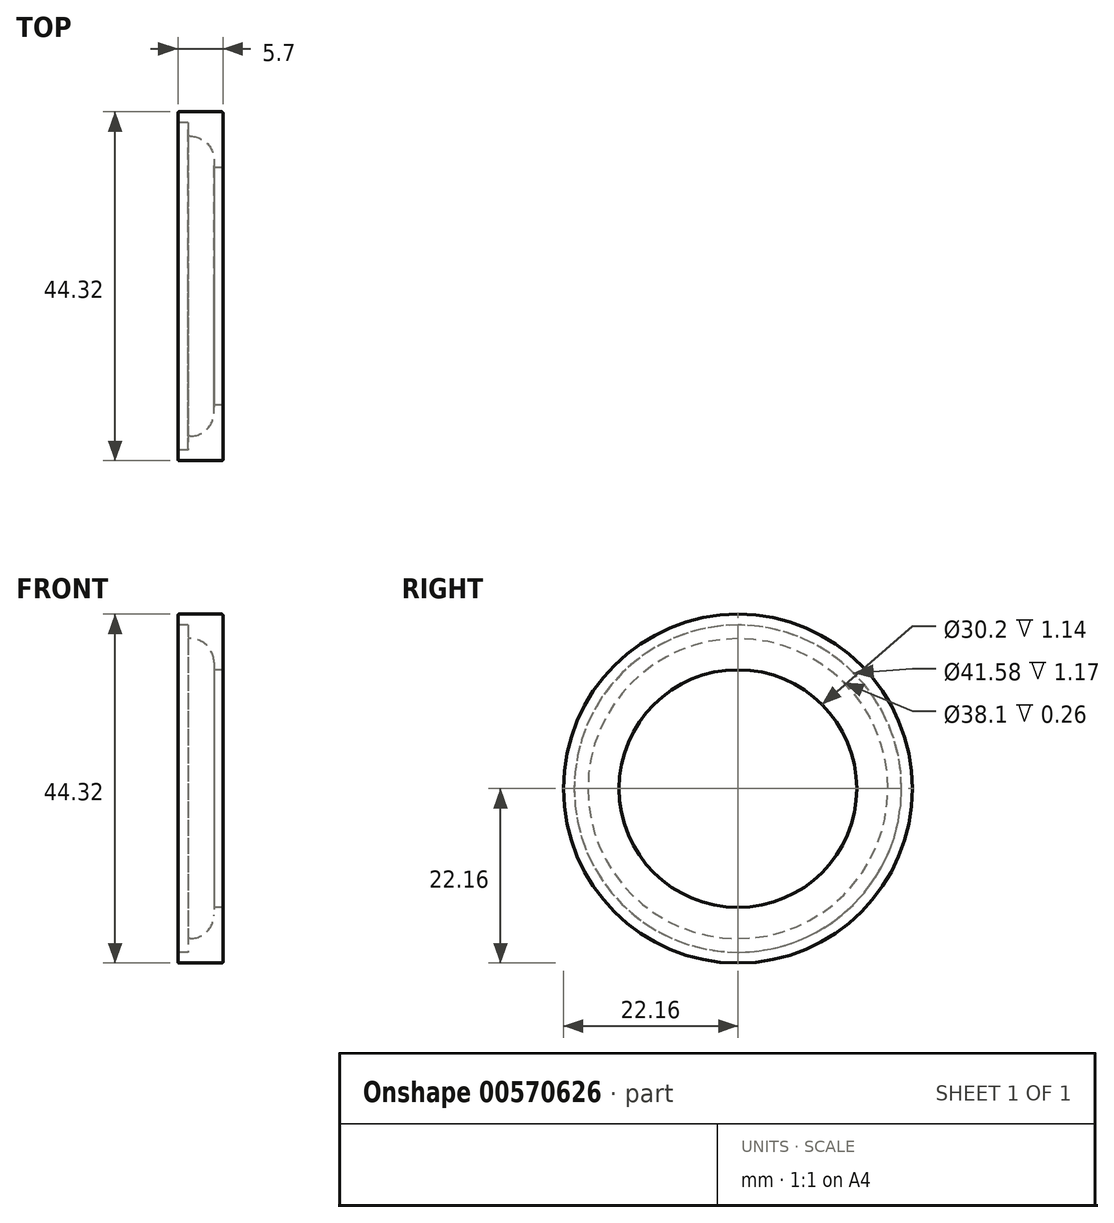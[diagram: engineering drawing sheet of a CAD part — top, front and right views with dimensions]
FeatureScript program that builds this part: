
annotation { "Feature Type Name" : "Feature", "Feature Type Description" : "" }
export const myFeature = defineFeature(function(context is Context, id is Id, definition is map)
    precondition{}
    {
        {
            var Q0;
            Q0=qCreatedBy(makeId("Top.planeOp"),FACE);
            var sketch = newSketch(context, id + "F0", { "sketchPlane" : qUnion([Q0])});
            skLineSegment(sketch, "E0", {"start": v(-3.39, 0) * mm, "end": v(17.46, 0) * mm, "construction": true});
            skLineSegment(sketch, "E1", {"start": v(7.3, 22.16) * mm, "end": v(1.6, 22.16) * mm});
            skLineSegment(sketch, "E2", {"start": v(7.3, 15.1) * mm, "end": v(7.3, 22.16) * mm});
            skLineSegment(sketch, "E3.right", {"start": v(1.6, 22.16) * mm, "end": v(1.6, 20.79) * mm});
            skLineSegment(sketch, "E4", {"start": v(1.6, 20.79) * mm, "end": v(2.9, 20.79) * mm});
            skLineSegment(sketch, "E5", {"start": v(2.9, 20.79) * mm, "end": v(2.9, 19.05) * mm});
            skLineSegment(sketch, "E6", {"start": v(2.9, 19.05) * mm, "end": v(3.16, 19.05) * mm});
            skLineSegment(sketch, "E7", {"start": v(6.16, 16.05) * mm, "end": v(6.16, 15.1) * mm});
            skLineSegment(sketch, "E8", {"start": v(6.16, 15.1) * mm, "end": v(7.3, 15.1) * mm});
            skLineSegment(sketch, "E9.MirrorCS", {"start": v(2.9, -20.8) * mm, "end": v(2.9, -19.05) * mm});
            skLineSegment(sketch, "E10.MirrorCS", {"start": v(6.16, -15.1) * mm, "end": v(7.3, -15.1) * mm});
            skLineSegment(sketch, "E11.MirrorCS", {"start": v(2.9, -19.05) * mm, "end": v(6.16, -19.05) * mm});
            skLineSegment(sketch, "E12.MirrorCS", {"start": v(1.6, -22.16) * mm, "end": v(1.6, -20.8) * mm});
            skLineSegment(sketch, "E13.MirrorCS", {"start": v(7.3, -22.16) * mm, "end": v(1.6, -22.16) * mm});
            skLineSegment(sketch, "E14.MirrorCS", {"start": v(6.16, -19.05) * mm, "end": v(6.16, -15.1) * mm});
            skLineSegment(sketch, "E15.MirrorCS", {"start": v(1.6, -20.8) * mm, "end": v(2.9, -20.79) * mm});
            skLineSegment(sketch, "E16.MirrorCS", {"start": v(7.3, -15.1) * mm, "end": v(7.3, -22.16) * mm});
            skArc(sketch, "E17.filletArc", {"start": v(6.16, 16.05) * mm, "mid": v(5.28, 18.17) * mm, "end": v(3.16, 19.05) * mm});
            skSolve(sketch);
        }
        {
            var Q0;
            Q0=makeQuery(id+"F0.imprint","IMPRINT",FACE,{"disambiguationData":[TD([[makeQuery(id+"F0.imprint","IMPRINT",EDGE,{"derivedFrom":sQuery(id+"F0.wireOp",EDGE,"E1")}),1.0]])]});
            var Q1;
            Q1=sQuery(id+"F0.wireOp",EDGE,"E0");
            revolve(context, id + "F1", {"entities" : qUnion([Q0]), "axis" : qUnion([Q1]), "revolveType" : RevolveType.FULL});
        }
        {
            var Q0;
            Q0=makeQuery(id+"F1.opRevolve","SWEPT_EDGE",EDGE,{"disambiguationData":[OSD([sQuery(id+"F0.wireOp",EDGE,"E3.top"),sQuery(id+"F0.wireOp",EDGE,"E3.right")])]});
            var Q1;
            Q1=makeQuery(id+"F1.opRevolve","SWEPT_EDGE",EDGE,{"disambiguationData":[OSD([sQuery(id+"F0.wireOp",EDGE,"RGYvIkMh-hPE8-4cA9-EaLV-vCRAY6uFLBn4"),sQuery(id+"F0.wireOp",EDGE,"QRPh4p4Z-RCfi-znFg-9l4J-0C2Ouf1ApQbl")])]});
            var Q2;
            Q2=makeQuery(id+"F1.opRevolve","SWEPT_EDGE",EDGE,{"disambiguationData":[OSD([sQuery(id+"F0.wireOp",EDGE,"E1"),sQuery(id+"F0.wireOp",EDGE,"E2")])]});
            var Q3;
            Q3=makeQuery(id+"F1.opRevolve","SWEPT_EDGE",EDGE,{"disambiguationData":[OSD([sQuery(id+"F0.wireOp",EDGE,"E1"),sQuery(id+"F0.wireOp",EDGE,"E3.right")])]});
            fillet(context, id + "F2", {"entities" : qUnion([Q0, Q1, Q2, Q3]), "radius" : 0.13 * mm, "tangentPropagation" : true, "allowEdgeOverflow" : false});
        }
    });
